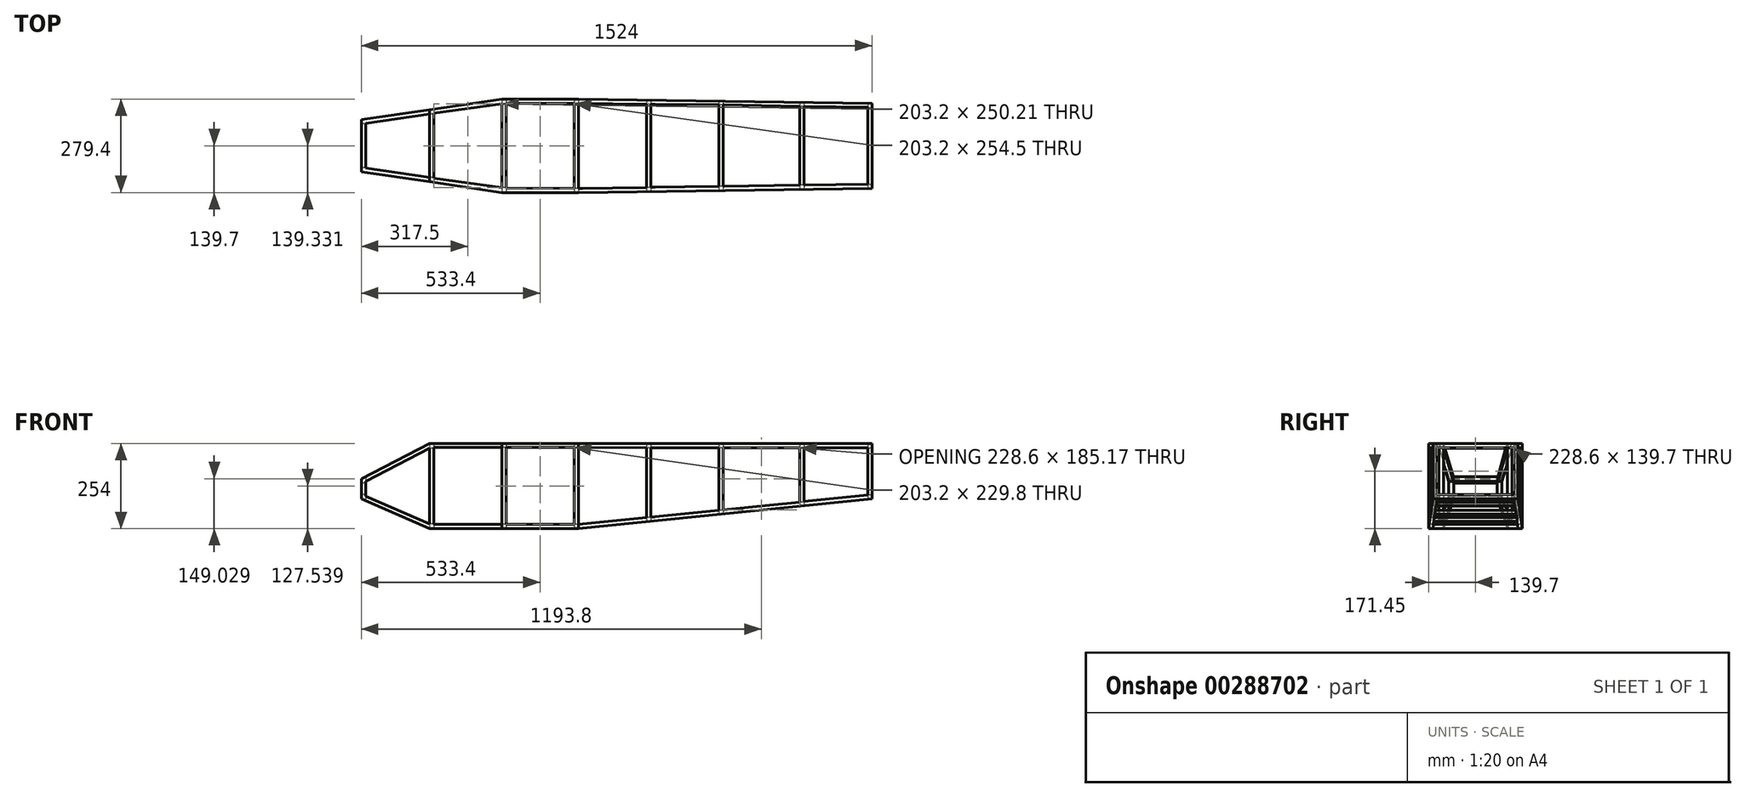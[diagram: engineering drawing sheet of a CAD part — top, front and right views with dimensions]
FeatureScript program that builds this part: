
annotation { "Feature Type Name" : "Feature", "Feature Type Description" : "" }
export const myFeature = defineFeature(function(context is Context, id is Id, definition is map)
    precondition{}
    {
        {
            var Q0;
            Q0=qCreatedBy(makeId("Top.planeOp"),FACE);
            var sketch = newSketch(context, id + "F0", { "sketchPlane" : qUnion([Q0])});
            skLineSegment(sketch, "E0.bottom", {"start": v(762, 177.8) * mm, "end": v(-762, 177.8) * mm});
            skLineSegment(sketch, "E0.top", {"start": v(762, -177.8) * mm, "end": v(-762, -177.8) * mm});
            skLineSegment(sketch, "E0.left", {"start": v(762, 177.8) * mm, "end": v(762, -177.8) * mm});
            skLineSegment(sketch, "E0.right", {"start": v(-762, 177.8) * mm, "end": v(-762, -177.8) * mm});
            skPoint(sketch, "E0.middle", {"position": v(0, 0) * mm});
            skSolve(sketch);
        }
        {
            var Q0;
            Q0=makeQuery(id+"F2.opExtrude","SWEPT_FACE",FACE,{"disambiguationData":[OSD([sQuery(id+"F0.wireOp",EDGE,"E0.top")])]});
            var sketch = newSketch(context, id + "F1", { "sketchPlane" : qUnion([Q0])});
            skLineSegment(sketch, "E1.0", {"start": v(-1003.3, -114.3) * mm, "end": v(1003.3, -114.3) * mm});
            skLineSegment(sketch, "E1.1", {"start": v(-1003.3, 114.3) * mm, "end": v(-1003.3, -114.3) * mm});
            skLineSegment(sketch, "E1.2", {"start": v(1003.3, 114.3) * mm, "end": v(-1003.3, 114.3) * mm});
            skLineSegment(sketch, "E1.3", {"start": v(1003.3, -114.3) * mm, "end": v(1003.3, 114.3) * mm});
            skSolve(sketch);
        }
        {
            var Q0;
            Q0=makeQuery(id+"F0.imprint","IMPRINT",FACE,{"disambiguationData":[TD([[makeQuery(id+"F0.imprint","IMPRINT",EDGE,{"derivedFrom":sQuery(id+"F0.wireOp",EDGE,"E0.bottom")}),1.0]])]});
            extrude(context, id + "F2", {"entities" : qUnion([Q0]), "endBound" : BoundingType.SYMMETRIC, "depth" : 254 * mm});
        }
        {
            var Q0;
            Q0=makeQuery(id+"F2.opExtrude","SWEPT_FACE",FACE,{"disambiguationData":[OSD([sQuery(id+"F0.wireOp",EDGE,"E0.left")])]});
            var sketch = newSketch(context, id + "F3", { "sketchPlane" : qUnion([Q0])});
            skLineSegment(sketch, "E2.0", {"start": v(-165.1, -114.3) * mm, "end": v(165.1, -114.3) * mm});
            skLineSegment(sketch, "E2.1", {"start": v(-165.1, 114.3) * mm, "end": v(-165.1, -114.3) * mm});
            skLineSegment(sketch, "E2.2", {"start": v(165.1, 114.3) * mm, "end": v(-165.1, 114.3) * mm});
            skLineSegment(sketch, "E2.3", {"start": v(165.1, -114.3) * mm, "end": v(165.1, 114.3) * mm});
            skSolve(sketch);
        }
        {
            var Q0;
            Q0=makeQuery(id+"F2.opExtrude","CAP_FACE",FACE,{"disambiguationData":[OSD([sQuery(id+"F0.wireOp",EDGE,"E0.bottom"),sQuery(id+"F0.wireOp",EDGE,"E0.top"),sQuery(id+"F0.wireOp",EDGE,"E0.left"),sQuery(id+"F0.wireOp",EDGE,"E0.right")])],"isStart":false});
            var sketch = newSketch(context, id + "F4", { "sketchPlane" : qUnion([Q0])});
            skLineSegment(sketch, "E3.0", {"start": v(-749.3, -165.1) * mm, "end": v(749.3, -165.1) * mm});
            skLineSegment(sketch, "E3.1", {"start": v(-749.3, 165.1) * mm, "end": v(-749.3, -165.1) * mm});
            skLineSegment(sketch, "E3.2", {"start": v(749.3, 165.1) * mm, "end": v(-749.3, 165.1) * mm});
            skLineSegment(sketch, "E3.3", {"start": v(749.3, -165.1) * mm, "end": v(749.3, 165.1) * mm});
            skSolve(sketch);
        }
        {
            var Q0;
            Q0=qCreatedBy(makeId("Front.planeOp"),FACE);
            var sketch = newSketch(context, id + "F5", { "sketchPlane" : qUnion([Q0])});
            skLineSegment(sketch, "E4.0", {"start": v(-762, 127) * mm, "end": v(-762, -127) * mm, "construction": true});
            skLineSegment(sketch, "E5.bottom", {"start": v(-558.8, -143.07) * mm, "end": v(-546.1, -143.07) * mm});
            skLineSegment(sketch, "E5.top", {"start": v(-558.8, 152.62) * mm, "end": v(-546.1, 152.62) * mm});
            skLineSegment(sketch, "E5.left", {"start": v(-558.8, -143.07) * mm, "end": v(-558.8, 152.62) * mm});
            skLineSegment(sketch, "E5.right", {"start": v(-546.1, -143.07) * mm, "end": v(-546.1, 152.62) * mm});
            skLineSegment(sketch, "E6.bottom", {"start": v(-342.9, -143.07) * mm, "end": v(-330.2, -143.07) * mm});
            skLineSegment(sketch, "E6.top", {"start": v(-342.9, 152.62) * mm, "end": v(-330.2, 152.62) * mm});
            skLineSegment(sketch, "E6.left", {"start": v(-342.9, -143.07) * mm, "end": v(-342.9, 152.62) * mm});
            skLineSegment(sketch, "E6.right", {"start": v(-330.2, -143.07) * mm, "end": v(-330.2, 152.62) * mm});
            skLineSegment(sketch, "E7.bottom", {"start": v(-127, -143.07) * mm, "end": v(-114.3, -143.07) * mm});
            skLineSegment(sketch, "E7.top", {"start": v(-127, 152.62) * mm, "end": v(-114.3, 152.62) * mm});
            skLineSegment(sketch, "E7.left", {"start": v(-127, -143.07) * mm, "end": v(-127, 152.62) * mm});
            skLineSegment(sketch, "E7.right", {"start": v(-114.3, -143.07) * mm, "end": v(-114.3, 152.62) * mm});
            skLineSegment(sketch, "E8.bottom", {"start": v(88.9, -143.07) * mm, "end": v(101.6, -143.07) * mm});
            skLineSegment(sketch, "E8.top", {"start": v(88.9, 152.62) * mm, "end": v(101.6, 152.62) * mm});
            skLineSegment(sketch, "E8.left", {"start": v(88.9, -143.07) * mm, "end": v(88.9, 152.62) * mm});
            skLineSegment(sketch, "E8.right", {"start": v(101.6, -143.07) * mm, "end": v(101.6, 152.62) * mm});
            skLineSegment(sketch, "E9", {"start": v(1356.57, 152.62) * mm, "end": v(-852.45, 152.62) * mm, "construction": true});
            skLineSegment(sketch, "E10", {"start": v(1396.25, -143.07) * mm, "end": v(-846.12, -143.07) * mm, "construction": true});
            skLineSegment(sketch, "E11.bottom", {"start": v(254, 152.62) * mm, "end": v(266.7, 152.62) * mm});
            skLineSegment(sketch, "E11.top", {"start": v(254, -143.07) * mm, "end": v(266.7, -143.07) * mm});
            skLineSegment(sketch, "E12.bottom", {"start": v(546.1, -143.07) * mm, "end": v(558.8, -143.07) * mm});
            skLineSegment(sketch, "E12.top", {"start": v(546.1, 152.62) * mm, "end": v(558.8, 152.62) * mm});
            skLineSegment(sketch, "E12.left", {"start": v(546.1, -143.07) * mm, "end": v(546.1, 152.62) * mm});
            skLineSegment(sketch, "E12.right", {"start": v(558.8, -143.07) * mm, "end": v(558.8, 152.62) * mm});
            skLineSegment(sketch, "E13.bottom", {"start": v(304.8, 152.62) * mm, "end": v(317.5, 152.62) * mm});
            skLineSegment(sketch, "E13.top", {"start": v(304.8, -143.07) * mm, "end": v(317.5, -143.07) * mm});
            skLineSegment(sketch, "E13.left", {"start": v(304.8, 152.62) * mm, "end": v(304.8, -143.07) * mm});
            skLineSegment(sketch, "E13.right", {"start": v(317.5, 152.62) * mm, "end": v(317.5, -143.07) * mm});
            skSolve(sketch);
        }
        {
            var Q0;
            Q0=qSketchRegion(id+"F5",true);
            extrude(context, id + "F6", {"entities" : qUnion([Q0]), "operationType" : NewBodyOperationType.ADD, "endBound" : BoundingType.SYMMETRIC, "depth" : 355.6 * mm});
        }
        {
            var Q0;
            Q0=qCreatedBy(makeId("Front.planeOp"),FACE);
            var sketch = newSketch(context, id + "F7", { "sketchPlane" : qUnion([Q0])});
            skLineSegment(sketch, "E14", {"start": v(-843.43, -20.57) * mm, "end": v(-558.8, 127) * mm});
            skLineSegment(sketch, "E15", {"start": v(-558.8, 127) * mm, "end": v(-1015.01, 307.35) * mm});
            skLineSegment(sketch, "E16", {"start": v(-1015.01, 307.35) * mm, "end": v(-843.43, -20.57) * mm});
            skLineSegment(sketch, "E17.0", {"start": v(-762, 127) * mm, "end": v(-762, -127) * mm, "construction": true});
            skLineSegment(sketch, "E18.0", {"start": v(762, 127) * mm, "end": v(762, -127) * mm, "construction": true});
            skLineSegment(sketch, "E19", {"start": v(-762, -38.1) * mm, "end": v(-558.8, -127) * mm});
            skLineSegment(sketch, "E20", {"start": v(-114.3, -127) * mm, "end": v(762, -38.1) * mm});
            skLineSegment(sketch, "E21", {"start": v(-762, -38.1) * mm, "end": v(-810.44, -38.1) * mm});
            skLineSegment(sketch, "E22", {"start": v(-810.44, -38.1) * mm, "end": v(-810.44, -218.05) * mm});
            skLineSegment(sketch, "E23", {"start": v(-810.44, -218.05) * mm, "end": v(819.71, -218.05) * mm});
            skLineSegment(sketch, "E24", {"start": v(819.71, -218.05) * mm, "end": v(819.71, -38.1) * mm});
            skLineSegment(sketch, "E25", {"start": v(819.71, -38.1) * mm, "end": v(762, -38.1) * mm});
            skLineSegment(sketch, "E26", {"start": v(-114.3, -127) * mm, "end": v(-558.8, -127) * mm});
            skSolve(sketch);
        }
        {
            var Q0;
            Q0=makeQuery(id+"F7.imprint","IMPRINT",FACE,{"disambiguationData":[TD([[makeQuery(id+"F7.imprint","IMPRINT",EDGE,{"derivedFrom":sQuery(id+"F7.wireOp",EDGE,"aae6dbfc-d4bc-4c02-a432-3037b792f5ca")}),1.0]])]});
            var Q1;
            Q1=makeQuery(id+"F7.imprint","IMPRINT",FACE,{"disambiguationData":[TD([[makeQuery(id+"F7.imprint","IMPRINT",EDGE,{"derivedFrom":sQuery(id+"F7.wireOp",EDGE,"E14")}),1.0]])]});
            var Q2;
            Q2=makeQuery(id+"F7.imprint","IMPRINT",FACE,{"disambiguationData":[TD([[makeQuery(id+"F7.imprint","IMPRINT",EDGE,{"derivedFrom":sQuery(id+"F7.wireOp",EDGE,"E19")}),-1.0]])]});
            extrude(context, id + "F8", {"entities" : qUnion([Q0, Q1, Q2]), "operationType" : NewBodyOperationType.REMOVE, "endBound" : BoundingType.SYMMETRIC, "oppositeDirection" : true, "depth" : 381 * mm});
        }
        {
            var Q0;
            Q0=qCreatedBy(makeId("Top.planeOp"),FACE);
            var sketch = newSketch(context, id + "F9", { "sketchPlane" : qUnion([Q0])});
            skLineSegment(sketch, "E27", {"start": v(-925.1, 0) * mm, "end": v(877.17, 0) * mm, "construction": true});
            skLineSegment(sketch, "E28", {"start": v(-885.68, 127) * mm, "end": v(840.74, 127) * mm, "construction": true});
            skLineSegment(sketch, "E29.0", {"start": v(-762, -177.8) * mm, "end": v(-762, 177.8) * mm, "construction": true});
            skLineSegment(sketch, "E30.0", {"start": v(762, 177.8) * mm, "end": v(762, -177.8) * mm, "construction": true});
            skLineSegment(sketch, "E31.0", {"start": v(-342.9, -406.4) * mm, "end": v(-342.9, -127) * mm, "construction": true});
            skLineSegment(sketch, "E32.0", {"start": v(101.6, -177.8) * mm, "end": v(101.6, 177.8) * mm, "construction": true});
            skLineSegment(sketch, "E33", {"start": v(762, 0) * mm, "end": v(762, 127) * mm});
            skLineSegment(sketch, "E34.0", {"start": v(-114.3, -177.8) * mm, "end": v(-114.3, 177.8) * mm, "construction": true});
            skLineSegment(sketch, "E35", {"start": v(-762, 77.57) * mm, "end": v(-762, 0) * mm});
            skLineSegment(sketch, "E36", {"start": v(-762, 0) * mm, "end": v(-762, 0) * mm});
            skLineSegment(sketch, "E37.MirrorCS", {"start": v(762, 0) * mm, "end": v(762, -127) * mm});
            skLineSegment(sketch, "E38.MirrorCS", {"start": v(-762, -77.57) * mm, "end": v(-762, 0) * mm});
            skLineSegment(sketch, "E39.MirrorCS", {"start": v(-885.68, -127) * mm, "end": v(840.74, -127) * mm, "construction": true});
            skLineSegment(sketch, "E40.MirrorCS", {"start": v(-762, 177.8) * mm, "end": v(-762, -177.8) * mm, "construction": true});
            skLineSegment(sketch, "E41.MirrorCS", {"start": v(762, -177.8) * mm, "end": v(762, 177.8) * mm, "construction": true});
            skLineSegment(sketch, "E42.MirrorCS", {"start": v(-342.9, 406.4) * mm, "end": v(-342.9, 127) * mm, "construction": true});
            skLineSegment(sketch, "E43.MirrorCS", {"start": v(-114.3, 177.8) * mm, "end": v(-114.3, -177.8) * mm, "construction": true});
            skLineSegment(sketch, "E44.MirrorCS", {"start": v(101.6, 177.8) * mm, "end": v(101.6, -177.8) * mm, "construction": true});
            skLineSegment(sketch, "E45.bottom", {"start": v(-858.41, 245.19) * mm, "end": v(858.29, 245.19) * mm});
            skLineSegment(sketch, "E45.top", {"start": v(-858.41, -226.45) * mm, "end": v(858.29, -226.45) * mm});
            skLineSegment(sketch, "E45.left", {"start": v(-858.41, 245.19) * mm, "end": v(-858.41, -226.45) * mm});
            skLineSegment(sketch, "E45.right", {"start": v(858.29, 245.19) * mm, "end": v(858.29, -226.45) * mm});
            skLineSegment(sketch, "E46", {"start": v(-342.9, 139.7) * mm, "end": v(-114.3, 139.7) * mm});
            skLineSegment(sketch, "E47.MirrorCS", {"start": v(-342.9, -139.7) * mm, "end": v(-114.3, -139.7) * mm});
            skLineSegment(sketch, "E48", {"start": v(-342.9, 139.7) * mm, "end": v(-762, 77.57) * mm});
            skLineSegment(sketch, "E49", {"start": v(-114.3, 139.7) * mm, "end": v(762, 127) * mm});
            skLineSegment(sketch, "E50", {"start": v(-342.9, -139.7) * mm, "end": v(-762, -77.57) * mm});
            skLineSegment(sketch, "E51", {"start": v(-114.3, -139.7) * mm, "end": v(762, -127) * mm});
            skSolve(sketch);
        }
        {
            var Q0;
            Q0=qSketchRegion(id+"F9",true);
            extrude(context, id + "F10", {"entities" : qUnion([Q0]), "operationType" : NewBodyOperationType.REMOVE, "endBound" : BoundingType.SYMMETRIC, "oppositeDirection" : true, "depth" : 381 * mm});
        }
        {
            var Q0;
            Q0=qCreatedBy(makeId("Top.planeOp"),FACE);
            var sketch = newSketch(context, id + "F11", { "sketchPlane" : qUnion([Q0])});
            skLineSegment(sketch, "E52.1", {"start": v(-749.29, -66.62) * mm, "end": v(-749.29, 66.82) * mm});
            skLineSegment(sketch, "E53.1", {"start": v(749.3, 114.99) * mm, "end": v(749.3, -114.99) * mm});
            skLineSegment(sketch, "E54.0", {"start": v(-127, 126.4) * mm, "end": v(-330.2, 126.88) * mm});
            skLineSegment(sketch, "E55.0", {"start": v(-330.2, -126.88) * mm, "end": v(-127, -127.62) * mm});
            skLineSegment(sketch, "E56.0", {"start": v(558.8, 117.24) * mm, "end": v(749.3, 114.48) * mm});
            skLineSegment(sketch, "E57.0", {"start": v(558.8, -117.24) * mm, "end": v(749.3, -114.48) * mm});
            skLineSegment(sketch, "E58.0", {"start": v(-749.29, -66.62) * mm, "end": v(-558.8, -94.86) * mm});
            skLineSegment(sketch, "E59", {"start": v(-342.9, -125.1) * mm, "end": v(-546.1, -96.69) * mm});
            skLineSegment(sketch, "E60", {"start": v(-546.1, 96.69) * mm, "end": v(-342.9, 125.1) * mm});
            skLineSegment(sketch, "E61.0.1", {"start": v(-546.1, -96.69) * mm, "end": v(-546.1, 96.69) * mm});
            skLineSegment(sketch, "E61.0.3", {"start": v(-558.8, 94.78) * mm, "end": v(-558.8, -94.86) * mm});
            skLineSegment(sketch, "E62.0.1", {"start": v(-342.9, 125.1) * mm, "end": v(-342.9, -125.1) * mm});
            skLineSegment(sketch, "E63.0.1", {"start": v(88.9, 124.23) * mm, "end": v(88.9, -124.5) * mm});
            skLineSegment(sketch, "E63.0.3", {"start": v(101.6, -124.3) * mm, "end": v(101.6, 124.05) * mm});
            skLineSegment(sketch, "E64.0.1", {"start": v(304.8, 122.67) * mm, "end": v(304.8, -121.36) * mm});
            skLineSegment(sketch, "E64.0.3", {"start": v(317.5, -120.83) * mm, "end": v(317.5, 122.5) * mm});
            skLineSegment(sketch, "E65.0.1", {"start": v(546.1, 117.12) * mm, "end": v(546.1, -117.44) * mm});
            skLineSegment(sketch, "E65.0.3", {"start": v(558.8, -117.24) * mm, "end": v(558.8, 117.24) * mm});
            skLineSegment(sketch, "E66.trimOffspring", {"start": v(304.8, -121.36) * mm, "end": v(101.6, -124.3) * mm});
            skLineSegment(sketch, "E67.trimOffspring", {"start": v(88.9, -124.5) * mm, "end": v(-114.3, -127.44) * mm});
            skLineSegment(sketch, "E68.trimOffspring", {"start": v(101.6, 124.05) * mm, "end": v(304.8, 122.67) * mm});
            skPoint(sketch, "E61.0.2.end.orphan", {"position": v(-558.8, 107.7) * mm});
            skPoint(sketch, "E61.0.2.start.orphan", {"position": v(-546.1, 109.58) * mm});
            skPoint(sketch, "E69.orphan", {"position": v(-558.8, -107.7) * mm});
            skPoint(sketch, "E70.orphan", {"position": v(-546.1, -109.58) * mm});
            skLineSegment(sketch, "E71", {"start": v(-749.29, 66.82) * mm, "end": v(-558.8, 94.78) * mm});
            skLineSegment(sketch, "E72", {"start": v(-114.3, -127.44) * mm, "end": v(-114.3, 126.4) * mm});
            skLineSegment(sketch, "E73", {"start": v(-330.2, 126.88) * mm, "end": v(-330.2, -126.88) * mm});
            skLineSegment(sketch, "E74", {"start": v(-127, 126.4) * mm, "end": v(-127, -127.62) * mm});
            skLineSegment(sketch, "E75", {"start": v(546.1, -117.44) * mm, "end": v(317.5, -120.83) * mm});
            skLineSegment(sketch, "E76", {"start": v(88.9, 124.23) * mm, "end": v(-114.3, 126.4) * mm});
            skLineSegment(sketch, "E77", {"start": v(546.1, 117.12) * mm, "end": v(317.5, 122.5) * mm});
            skSolve(sketch);
        }
        {
            var Q0;
            Q0=qSketchRegion(id+"F11",true);
            extrude(context, id + "F12", {"entities" : qUnion([Q0]), "operationType" : NewBodyOperationType.REMOVE, "endBound" : BoundingType.SYMMETRIC, "depth" : 381 * mm});
        }
        {
            var Q0;
            Q0=qCreatedBy(makeId("Front.planeOp"),FACE);
            var sketch = newSketch(context, id + "F13", { "sketchPlane" : qUnion([Q0])});
            skLineSegment(sketch, "E78.0", {"start": v(-749.3, 13.93) * mm, "end": v(-558.8, 112.7) * mm});
            skLineSegment(sketch, "E78.1", {"start": v(-749.3, -29.8) * mm, "end": v(-749.3, 13.93) * mm});
            skLineSegment(sketch, "E78.2", {"start": v(-749.3, -29.8) * mm, "end": v(-558.8, -113.14) * mm});
            skLineSegment(sketch, "E78.3", {"start": v(-342.9, -114.3) * mm, "end": v(-546.1, -114.3) * mm});
            skLineSegment(sketch, "E79.0", {"start": v(749.3, -26.62) * mm, "end": v(558.8, -45.95) * mm});
            skLineSegment(sketch, "E79.1", {"start": v(749.3, -26.62) * mm, "end": v(749.3, 114.3) * mm});
            skLineSegment(sketch, "E79.2", {"start": v(558.8, 114.3) * mm, "end": v(749.3, 114.3) * mm});
            skLineSegment(sketch, "E80", {"start": v(-127, -114.36) * mm, "end": v(-330.2, -114.3) * mm});
            skLineSegment(sketch, "E81.0.1", {"start": v(558.8, 114.3) * mm, "end": v(558.8, -45.95) * mm});
            skLineSegment(sketch, "E82.0.1", {"start": v(101.6, 114.89) * mm, "end": v(101.6, -92.46) * mm});
            skLineSegment(sketch, "E82.0.3", {"start": v(304.8, -71.84) * mm, "end": v(304.8, 114.63) * mm});
            skLineSegment(sketch, "E83.0.0", {"start": v(-330.2, 115.44) * mm, "end": v(-330.2, -114.3) * mm});
            skLineSegment(sketch, "E83.0.2", {"start": v(-127, -114.36) * mm, "end": v(-127, 115.18) * mm});
            skLineSegment(sketch, "E84.0.1", {"start": v(-546.1, 115.71) * mm, "end": v(-546.1, -114.3) * mm});
            skLineSegment(sketch, "E84.0.3", {"start": v(-342.9, -114.3) * mm, "end": v(-342.9, 115.45) * mm});
            skLineSegment(sketch, "E85.0.2", {"start": v(-558.8, -113.14) * mm, "end": v(-558.8, 112.7) * mm});
            skPoint(sketch, "E81.0.0.start.orphan", {"position": v(749.3, 127) * mm});
            skPoint(sketch, "E86.orphan", {"position": v(558.8, 127) * mm});
            skPoint(sketch, "E87.0.0.start.orphan", {"position": v(558.8, 126.99) * mm});
            skLineSegment(sketch, "E88.trimOffspring", {"start": v(304.8, 114.63) * mm, "end": v(101.6, 114.89) * mm});
            skPoint(sketch, "E82.0.0.start.orphan", {"position": v(304.8, 127) * mm});
            skLineSegment(sketch, "E89.trimOffspring", {"start": v(-127, 115.18) * mm, "end": v(-330.2, 115.44) * mm});
            skPoint(sketch, "E83.0.1.end.orphan", {"position": v(-127, -127) * mm});
            skPoint(sketch, "E90.orphan", {"position": v(-330.2, -127) * mm});
            skLineSegment(sketch, "E91.trimOffspring", {"start": v(-342.9, 115.45) * mm, "end": v(-546.1, 115.71) * mm});
            skPoint(sketch, "E83.0.3.end.orphan", {"position": v(-330.2, 127) * mm});
            skPoint(sketch, "E83.0.3.start.orphan", {"position": v(-127, 127) * mm});
            skPoint(sketch, "E84.0.2.end.orphan", {"position": v(-342.9, -127) * mm});
            skPoint(sketch, "E92.orphan", {"position": v(-546.1, -127) * mm});
            skPoint(sketch, "E93.orphan", {"position": v(-546.1, 127) * mm});
            skPoint(sketch, "E85.0.3.start.orphan", {"position": v(-558.8, 127) * mm});
            skPoint(sketch, "E94.orphan", {"position": v(101.6, 127) * mm});
            skLineSegment(sketch, "E95", {"start": v(546.1, -48.1) * mm, "end": v(456.3, -56.47) * mm});
            skPoint(sketch, "E81.0.2.end.orphan", {"position": v(749.3, -39.39) * mm});
            skPoint(sketch, "E96.orphan", {"position": v(-342.9, 127) * mm});
            skLineSegment(sketch, "E97.left", {"start": v(-680.76, 244.02) * mm, "end": v(-680.76, 242.67) * mm});
            skLineSegment(sketch, "E97.right", {"start": v(-640.08, 244.02) * mm, "end": v(-640.08, 242.67) * mm});
            skLineSegment(sketch, "E98.bottom", {"start": v(851.63, 270.75) * mm, "end": v(-718.73, 270.75) * mm});
            skLineSegment(sketch, "E98.top", {"start": v(851.63, 127) * mm, "end": v(-718.73, 127) * mm});
            skLineSegment(sketch, "E98.left", {"start": v(851.63, 270.75) * mm, "end": v(851.63, 127) * mm});
            skLineSegment(sketch, "E98.right", {"start": v(-718.73, 270.75) * mm, "end": v(-718.73, 127) * mm});
            skLineSegment(sketch, "E99", {"start": v(-114.3, -114.36) * mm, "end": v(88.9, -93.75) * mm});
            skLineSegment(sketch, "E100", {"start": v(546.1, 114.3) * mm, "end": v(317.5, 114.61) * mm});
            skLineSegment(sketch, "E101", {"start": v(88.9, 114.9) * mm, "end": v(-114.3, 115.18) * mm});
            skLineSegment(sketch, "E102", {"start": v(-114.3, 115.18) * mm, "end": v(-114.3, -114.36) * mm});
            skLineSegment(sketch, "E103", {"start": v(88.9, 114.9) * mm, "end": v(88.9, -93.75) * mm});
            skLineSegment(sketch, "E104", {"start": v(317.5, 114.61) * mm, "end": v(317.5, -70.55) * mm});
            skLineSegment(sketch, "E105", {"start": v(546.1, 114.3) * mm, "end": v(546.1, -48.1) * mm});
            skLineSegment(sketch, "E106.trimOffspring", {"start": v(317.5, -70.55) * mm, "end": v(456.3, -56.47) * mm});
            skLineSegment(sketch, "E107.trimOffspring", {"start": v(101.6, -92.46) * mm, "end": v(304.8, -71.84) * mm});
            skSolve(sketch);
        }
        {
            var Q0;
            Q0=qSketchRegion(id+"F13",true);
            extrude(context, id + "F14", {"entities" : qUnion([Q0]), "operationType" : NewBodyOperationType.REMOVE, "endBound" : BoundingType.SYMMETRIC, "oppositeDirection" : true, "depth" : 381 * mm});
        }
        {
            var Q0;
            {var subQ4=sQuery(id+"F5.wireOp",EDGE,"E5.top");var subQ11=sQuery(id+"F5.wireOp",EDGE,"E5.left");Q0=makeQuery(id+"F14.boolean.opBoolean","MERGE",FACE,{"derivedFrom":[makeQuery(id+"F12.boolean.opBoolean","MERGE",FACE,{"derivedFrom":[makeQuery(id+"F6.boolean.opBoolean","SPLIT",FACE,{"disambiguationData":[TD([makeQuery(id+"F6.opExtrude","SWEPT_FACE",FACE,{"disambiguationData":[OSD([subQ4])]})])],"derivedFrom":makeQuery(id+"F6.opExtrude","SWEPT_FACE",FACE,{"disambiguationData":[OSD([subQ11])]})}),makeQuery(id+"F12.opExtrude","SWEPT_FACE",FACE,{"disambiguationData":[OSD([sQuery(id+"F11.wireOp",EDGE,"76c89935-962c-43c5-8293-adbbc792d1c5.0")])]})]}),makeQuery(id+"F14.opExtrude","SWEPT_FACE",FACE,{"disambiguationData":[OSD([sQuery(id+"F13.wireOp",EDGE,"9ef2c277-a94d-4be6-9fd4-f6ea86bf56da.0.3")])]})]});}
            var sketch = newSketch(context, id + "F15", { "sketchPlane" : qUnion([Q0])});
            skLineSegment(sketch, "E108.bottom", {"start": v(-94.78, 112.7) * mm, "end": v(94.86, 112.7) * mm});
            skLineSegment(sketch, "E108.top", {"start": v(-94.78, -113.14) * mm, "end": v(94.86, -113.14) * mm});
            skLineSegment(sketch, "E108.left", {"start": v(-94.78, 112.7) * mm, "end": v(-94.78, -113.14) * mm});
            skLineSegment(sketch, "E108.right", {"start": v(94.86, 112.7) * mm, "end": v(94.86, -113.14) * mm});
            skSolve(sketch);
        }
        {
            var Q0;
            Q0=qSketchRegion(id+"F15",true);
            extrude(context, id + "F16", {"entities" : qUnion([Q0]), "operationType" : NewBodyOperationType.REMOVE, "oppositeDirection" : true, "depth" : 25.4 * mm});
        }
        {
            var Q0;
            {var subQ1=sQuery(id+"F5.wireOp",EDGE,"E6.left");var subQ2=sQuery(id+"F5.wireOp",EDGE,"E6.top");Q0=makeQuery(id+"F14.boolean.opBoolean","MERGE",FACE,{"derivedFrom":[makeQuery(id+"F12.boolean.opBoolean","MERGE",FACE,{"derivedFrom":[makeQuery(id+"F6.boolean.opBoolean","SPLIT",FACE,{"disambiguationData":[TD([makeQuery(id+"F6.opExtrude","SWEPT_FACE",FACE,{"disambiguationData":[OSD([subQ2])]})])],"derivedFrom":makeQuery(id+"F6.opExtrude","SWEPT_FACE",FACE,{"disambiguationData":[OSD([subQ1])]})}),makeQuery(id+"F12.opExtrude","SWEPT_FACE",FACE,{"disambiguationData":[OSD([sQuery(id+"F11.wireOp",EDGE,"7b3102ac-ed15-4f5d-bc17-57cfcd7eebf1.0")])]})]}),makeQuery(id+"F14.opExtrude","SWEPT_FACE",FACE,{"disambiguationData":[OSD([sQuery(id+"F13.wireOp",EDGE,"8vpACN4d-Oada-hr1t-Xb63-NezVnV2j5PEM")])]})]});}
            var sketch = newSketch(context, id + "F17", { "sketchPlane" : qUnion([Q0])});
            skLineSegment(sketch, "E109.bottom", {"start": v(-125.1, 115.45) * mm, "end": v(125.1, 115.45) * mm});
            skLineSegment(sketch, "E109.top", {"start": v(-125.1, -114.3) * mm, "end": v(125.1, -114.3) * mm});
            skLineSegment(sketch, "E109.left", {"start": v(-125.1, 115.45) * mm, "end": v(-125.1, -114.3) * mm});
            skLineSegment(sketch, "E109.right", {"start": v(125.1, 115.45) * mm, "end": v(125.1, -114.3) * mm});
            skSolve(sketch);
        }
        {
            var Q0;
            Q0=qSketchRegion(id+"F17",true);
            extrude(context, id + "F18", {"entities" : qUnion([Q0]), "operationType" : NewBodyOperationType.REMOVE, "oppositeDirection" : true, "depth" : 25.4 * mm});
        }
        {
            var Q0;
            {var subQ8=sQuery(id+"F5.wireOp",EDGE,"E7.top");var subQ16=sQuery(id+"F5.wireOp",EDGE,"E7.left");Q0=makeQuery(id+"F14.boolean.opBoolean","MERGE",FACE,{"derivedFrom":[makeQuery(id+"F12.boolean.opBoolean","MERGE",FACE,{"derivedFrom":[makeQuery(id+"F6.boolean.opBoolean","SPLIT",FACE,{"disambiguationData":[TD([makeQuery(id+"F6.opExtrude","SWEPT_FACE",FACE,{"disambiguationData":[OSD([subQ8])]})])],"derivedFrom":makeQuery(id+"F6.opExtrude","SWEPT_FACE",FACE,{"disambiguationData":[OSD([subQ16])]})}),makeQuery(id+"F12.opExtrude","SWEPT_FACE",FACE,{"disambiguationData":[OSD([sQuery(id+"F11.wireOp",EDGE,"b35c1112-db7b-4928-a18e-9a17467dcdab.0")])]})]}),makeQuery(id+"F14.opExtrude","SWEPT_FACE",FACE,{"disambiguationData":[OSD([sQuery(id+"F13.wireOp",EDGE,"fa40cc79-636a-4cbc-a25d-f27d8fe22ac2.0.3")])]})]});}
            var sketch = newSketch(context, id + "F19", { "sketchPlane" : qUnion([Q0])});
            skLineSegment(sketch, "E110.bottom", {"start": v(-126.4, 115.18) * mm, "end": v(127.62, 115.18) * mm});
            skLineSegment(sketch, "E110.top", {"start": v(-126.4, -114.36) * mm, "end": v(127.62, -114.36) * mm});
            skLineSegment(sketch, "E110.left", {"start": v(-126.4, 115.18) * mm, "end": v(-126.4, -114.36) * mm});
            skLineSegment(sketch, "E110.right", {"start": v(127.62, 115.18) * mm, "end": v(127.62, -114.36) * mm});
            skSolve(sketch);
        }
        {
            var Q0;
            Q0=qSketchRegion(id+"F19",true);
            extrude(context, id + "F20", {"entities" : qUnion([Q0]), "operationType" : NewBodyOperationType.REMOVE, "oppositeDirection" : true, "depth" : 25.4 * mm});
        }
        {
            var Q0;
            {var subQ0=sQuery(id+"F5.wireOp",EDGE,"E8.bottom");var subQ36=sQuery(id+"F5.wireOp",EDGE,"E8.left");var subQ37=sQuery(id+"F5.wireOp",EDGE,"E8.top");var subQ60=makeQuery(id+"F6.opExtrude","SWEPT_FACE",FACE,{"disambiguationData":[OSD([subQ36])]});Q0=makeQuery(id+"F14.boolean.opBoolean","MERGE",FACE,{"derivedFrom":[makeQuery(id+"F12.boolean.opBoolean","MERGE",FACE,{"derivedFrom":[makeQuery(id+"F6.boolean.opBoolean","SPLIT",FACE,{"disambiguationData":[TD([makeQuery(id+"F6.opExtrude","SWEPT_FACE",FACE,{"disambiguationData":[OSD([subQ37])]})])],"derivedFrom":subQ60}),makeQuery(id+"F6.boolean.opBoolean","SPLIT",FACE,{"disambiguationData":[TD([makeQuery(id+"F6.opExtrude","SWEPT_FACE",FACE,{"disambiguationData":[OSD([subQ0])]})])],"derivedFrom":subQ60}),makeQuery(id+"F12.opExtrude","SWEPT_FACE",FACE,{"disambiguationData":[OSD([sQuery(id+"F11.wireOp",EDGE,"7310f20e-b108-4276-8773-8cf4f74fe12c.0")])]})]}),makeQuery(id+"F14.opExtrude","SWEPT_FACE",FACE,{"disambiguationData":[OSD([sQuery(id+"F13.wireOp",EDGE,"FrRoJ9V7-tiAn-pTb4-UzEj-WxOpO9FH2ecp")])]})]});}
            var sketch = newSketch(context, id + "F21", { "sketchPlane" : qUnion([Q0])});
            skLineSegment(sketch, "E111.bottom", {"start": v(-124.23, 114.9) * mm, "end": v(124.5, 114.9) * mm});
            skLineSegment(sketch, "E111.top", {"start": v(-124.23, -93.75) * mm, "end": v(124.5, -93.75) * mm});
            skLineSegment(sketch, "E111.left", {"start": v(-124.23, 114.9) * mm, "end": v(-124.23, -93.75) * mm});
            skLineSegment(sketch, "E111.right", {"start": v(124.5, 114.9) * mm, "end": v(124.5, -93.75) * mm});
            skSolve(sketch);
        }
        {
            var Q0;
            Q0=qSketchRegion(id+"F21",true);
            extrude(context, id + "F22", {"entities" : qUnion([Q0]), "operationType" : NewBodyOperationType.REMOVE, "oppositeDirection" : true, "depth" : 25.4 * mm});
        }
        {
            var Q0;
            {var subQ35=sQuery(id+"F5.wireOp",EDGE,"E13.left");var subQ37=sQuery(id+"F5.wireOp",EDGE,"E13.bottom");Q0=makeQuery(id+"F14.boolean.opBoolean","MERGE",FACE,{"derivedFrom":[makeQuery(id+"F12.boolean.opBoolean","MERGE",FACE,{"derivedFrom":[makeQuery(id+"F6.boolean.opBoolean","SPLIT",FACE,{"disambiguationData":[TD([makeQuery(id+"F6.opExtrude","SWEPT_FACE",FACE,{"disambiguationData":[OSD([subQ37])]})])],"derivedFrom":makeQuery(id+"F6.opExtrude","SWEPT_FACE",FACE,{"disambiguationData":[OSD([subQ35])]})}),makeQuery(id+"F12.opExtrude","SWEPT_FACE",FACE,{"disambiguationData":[OSD([sQuery(id+"F11.wireOp",EDGE,"b7ba8543-acbf-43cf-88d8-2159336d2e7e.0")])]})]}),makeQuery(id+"F14.opExtrude","SWEPT_FACE",FACE,{"disambiguationData":[OSD([sQuery(id+"F13.wireOp",EDGE,"MzW9eNza-KUkf-pAGu-OPrh-YCygVrhiN9A4")])]})]});}
            var sketch = newSketch(context, id + "F23", { "sketchPlane" : qUnion([Q0])});
            skLineSegment(sketch, "E112.bottom", {"start": v(-122.67, 114.63) * mm, "end": v(121.36, 114.63) * mm});
            skLineSegment(sketch, "E112.top", {"start": v(-122.67, -71.84) * mm, "end": v(121.36, -71.84) * mm});
            skLineSegment(sketch, "E112.left", {"start": v(-122.67, 114.63) * mm, "end": v(-122.67, -71.84) * mm});
            skLineSegment(sketch, "E112.right", {"start": v(121.36, 114.63) * mm, "end": v(121.36, -71.84) * mm});
            skSolve(sketch);
        }
        {
            var Q0;
            Q0=qSketchRegion(id+"F23",true);
            extrude(context, id + "F24", {"entities" : qUnion([Q0]), "operationType" : NewBodyOperationType.REMOVE, "oppositeDirection" : true, "depth" : 15.24 * mm});
        }
        {
            var Q0;
            {var subQ18=sQuery(id+"F5.wireOp",EDGE,"E12.left");var subQ19=sQuery(id+"F5.wireOp",EDGE,"E12.top");Q0=makeQuery(id+"F14.boolean.opBoolean","MERGE",FACE,{"derivedFrom":[makeQuery(id+"F12.boolean.opBoolean","MERGE",FACE,{"derivedFrom":[makeQuery(id+"F6.boolean.opBoolean","SPLIT",FACE,{"disambiguationData":[TD([makeQuery(id+"F6.opExtrude","SWEPT_FACE",FACE,{"disambiguationData":[OSD([subQ19])]})])],"derivedFrom":makeQuery(id+"F6.opExtrude","SWEPT_FACE",FACE,{"disambiguationData":[OSD([subQ18])]})}),makeQuery(id+"F12.opExtrude","SWEPT_FACE",FACE,{"disambiguationData":[OSD([sQuery(id+"F11.wireOp",EDGE,"94f42aec-5a63-4bb3-a17e-c23af455982a.0")])]})]}),makeQuery(id+"F14.opExtrude","SWEPT_FACE",FACE,{"disambiguationData":[OSD([sQuery(id+"F13.wireOp",EDGE,"4bo9Z2lR-88Dg-C45D-lGNA-9ZzvTnCFj7b6")])]})]});}
            var sketch = newSketch(context, id + "F25", { "sketchPlane" : qUnion([Q0])});
            skLineSegment(sketch, "E113.bottom", {"start": v(-117.12, 114.3) * mm, "end": v(117.44, 114.3) * mm});
            skLineSegment(sketch, "E113.top", {"start": v(-117.12, -48.1) * mm, "end": v(117.44, -48.1) * mm});
            skLineSegment(sketch, "E113.left", {"start": v(117.44, 114.3) * mm, "end": v(117.44, -48.1) * mm});
            skLineSegment(sketch, "E113.right", {"start": v(-117.12, 114.3) * mm, "end": v(-117.12, -48.1) * mm});
            skSolve(sketch);
        }
        {
            var Q0;
            Q0=qSketchRegion(id+"F25",true);
            extrude(context, id + "F26", {"entities" : qUnion([Q0]), "operationType" : NewBodyOperationType.REMOVE, "oppositeDirection" : true, "depth" : 13.97 * mm});
        }
        {
            var Q0;
            Q0=makeQuery(id+"F14.boolean.opBoolean","MERGE",FACE,{"derivedFrom":[makeQuery(id+"F12.boolean.opBoolean","COPY",FACE,{"derivedFrom":makeQuery(id+"F12.opExtrude","SWEPT_FACE",FACE,{"disambiguationData":[OSD([sQuery(id+"F11.wireOp",EDGE,"adecc727-4d20-49de-aa06-e82a0813468d.1")])]})}),makeQuery(id+"F14.opExtrude","SWEPT_FACE",FACE,{"disambiguationData":[OSD([sQuery(id+"F13.wireOp",EDGE,"9f7ba322-1395-4fc7-9540-b671459040af.2")])]})]});
            var sketch = newSketch(context, id + "F27", { "sketchPlane" : qUnion([Q0])});
            skLineSegment(sketch, "E114.bottom", {"start": v(-114.91, 114.3) * mm, "end": v(114.6, 114.3) * mm});
            skLineSegment(sketch, "E114.top", {"start": v(-114.91, -7.58) * mm, "end": v(114.6, -7.58) * mm});
            skLineSegment(sketch, "E114.left", {"start": v(-114.91, 114.3) * mm, "end": v(-114.91, -7.58) * mm});
            skLineSegment(sketch, "E114.right", {"start": v(114.6, 114.3) * mm, "end": v(114.6, -7.58) * mm});
            skSolve(sketch);
        }
        {
            var Q0;
            Q0=makeQuery(id+"F2.opExtrude","SWEPT_FACE",FACE,{"disambiguationData":[OSD([sQuery(id+"F0.wireOp",EDGE,"E0.right")])]});
            var sketch = newSketch(context, id + "F28", { "sketchPlane" : qUnion([Q0])});
            skLineSegment(sketch, "E115.0", {"start": v(-64.87, 8.95) * mm, "end": v(64.87, 8.95) * mm});
            skLineSegment(sketch, "E116.0", {"start": v(-64.87, -25.4) * mm, "end": v(-64.87, 8.95) * mm});
            skLineSegment(sketch, "E116.1", {"start": v(-64.87, -25.4) * mm, "end": v(64.87, -25.4) * mm});
            skLineSegment(sketch, "E116.2", {"start": v(64.87, -25.4) * mm, "end": v(64.87, 8.95) * mm});
            skSolve(sketch);
        }
        {
            var Q0;
            Q0=qSketchRegion(id+"F28",true);
            extrude(context, id + "F29", {"entities" : qUnion([Q0]), "operationType" : NewBodyOperationType.REMOVE, "oppositeDirection" : true, "depth" : 25.4 * mm});
        }
        {
            var Q0;
            Q0=makeQuery(id+"F2.opExtrude","SWEPT_FACE",FACE,{"disambiguationData":[OSD([sQuery(id+"F0.wireOp",EDGE,"E0.left")])]});
            var sketch = newSketch(context, id + "F30", { "sketchPlane" : qUnion([Q0])});
            skLineSegment(sketch, "E117.bottom", {"start": v(-114.3, 114.3) * mm, "end": v(114.3, 114.3) * mm});
            skLineSegment(sketch, "E117.top", {"start": v(-114.3, -25.4) * mm, "end": v(114.3, -25.4) * mm});
            skLineSegment(sketch, "E117.left", {"start": v(-114.3, 114.3) * mm, "end": v(-114.3, -25.4) * mm});
            skLineSegment(sketch, "E117.right", {"start": v(114.3, 114.3) * mm, "end": v(114.3, -25.4) * mm});
            skSolve(sketch);
        }
        {
            var Q0;
            Q0=makeQuery(id+"F30.imprint","IMPRINT",FACE,{"disambiguationData":[TD([[makeQuery(id+"F30.imprint","IMPRINT",EDGE,{"derivedFrom":sQuery(id+"F30.wireOp",EDGE,"E117.bottom")}),-1.0]])]});
            extrude(context, id + "F31", {"entities" : qUnion([Q0]), "operationType" : NewBodyOperationType.REMOVE, "oppositeDirection" : true, "depth" : 12.7 * mm});
        }
    });
